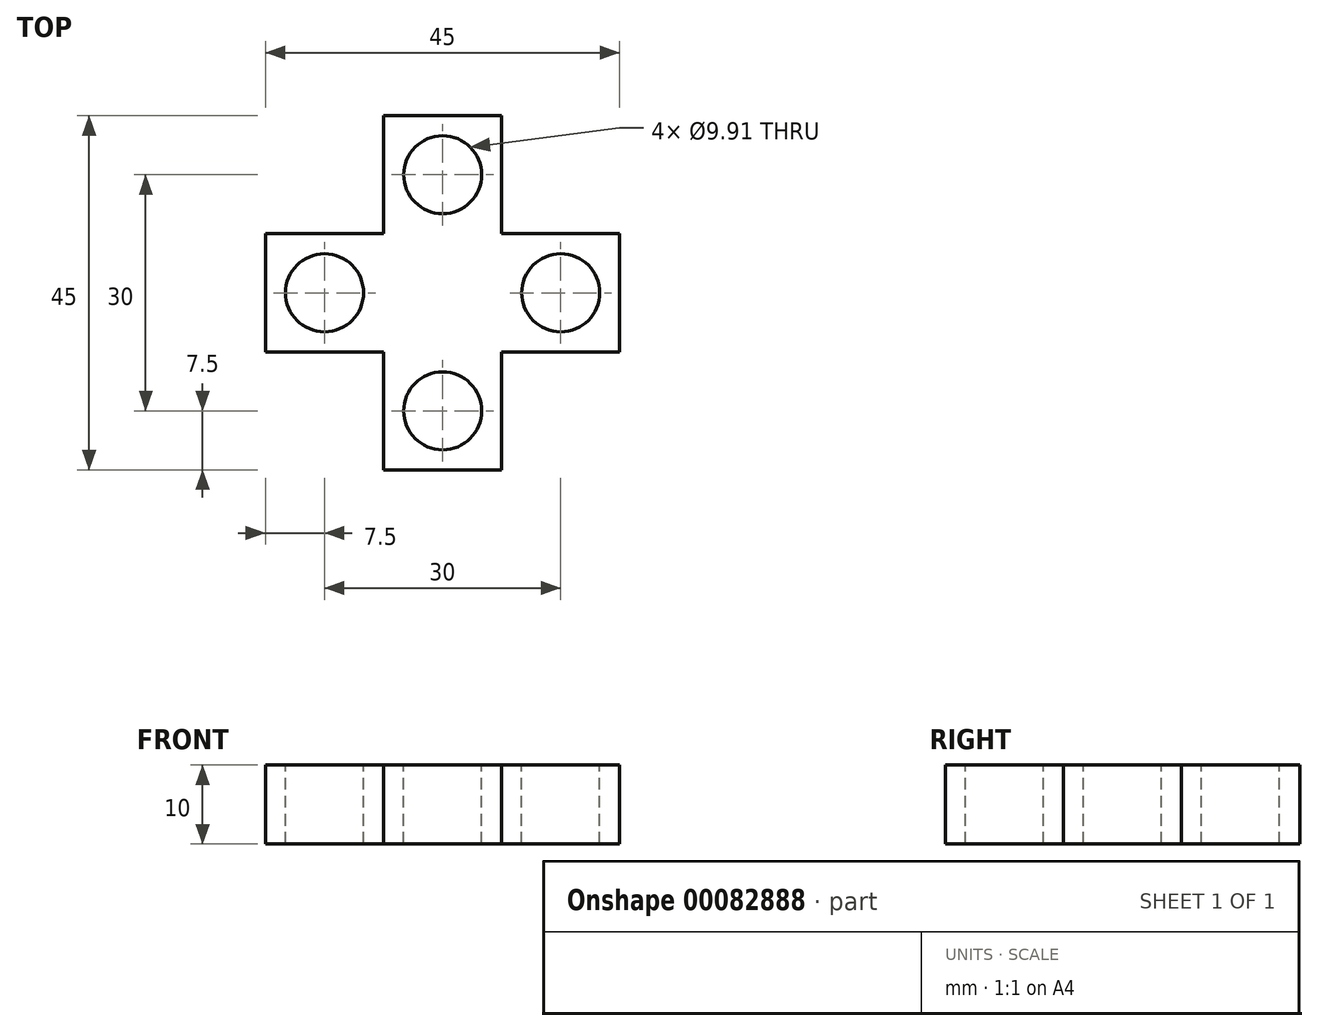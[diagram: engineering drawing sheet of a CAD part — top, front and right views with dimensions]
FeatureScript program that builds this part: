
annotation { "Feature Type Name" : "Feature", "Feature Type Description" : "" }
export const myFeature = defineFeature(function(context is Context, id is Id, definition is map)
    precondition{}
    {
        {
            var Q0;
            Q0=qCreatedBy(makeId("Top.planeOp"),FACE);
            var sketch = newSketch(context, id + "F0", { "sketchPlane" : qUnion([Q0])});
            skLineSegment(sketch, "E0.bottom", {"start": v(22.5, 7.5) * mm, "end": v(-22.5, 7.5) * mm});
            skLineSegment(sketch, "E0.top", {"start": v(22.5, -7.5) * mm, "end": v(-22.5, -7.5) * mm});
            skLineSegment(sketch, "E0.left", {"start": v(22.5, 7.5) * mm, "end": v(22.5, -7.5) * mm});
            skLineSegment(sketch, "E0.right", {"start": v(-22.5, 7.5) * mm, "end": v(-22.5, -7.5) * mm});
            skPoint(sketch, "E0.middle", {"position": v(0, 0) * mm});
            skLineSegment(sketch, "E1.bottom", {"start": v(-7.5, 22.5) * mm, "end": v(7.5, 22.5) * mm});
            skLineSegment(sketch, "E1.top", {"start": v(-7.5, -22.5) * mm, "end": v(7.5, -22.5) * mm});
            skLineSegment(sketch, "E1.left", {"start": v(-7.5, 22.5) * mm, "end": v(-7.5, -22.5) * mm});
            skLineSegment(sketch, "E1.right", {"start": v(7.5, 22.5) * mm, "end": v(7.5, -22.5) * mm});
            skSolve(sketch);
        }
        {
            var Q0;
            {var subQ0=sQuery(id+"F0.wireOp",EDGE,"E0.right");Q0=makeQuery(id+"F0.imprint","IMPRINT",FACE,{"disambiguationData":[TD([[makeQuery(id+"F0.imprint","IMPRINT",EDGE,{"derivedFrom":subQ0}),1.0]])]});}
            var Q1;
            {var subQ0=sQuery(id+"F0.wireOp",EDGE,"E1.right");var subQ1=sQuery(id+"F0.wireOp",EDGE,"E0.bottom");var subQ2=makeQuery(id+"F0.imprint","INTERSECT",VERTEX,{"derivedFrom":[subQ1,subQ0]});Q1=makeQuery(id+"F0.imprint","IMPRINT",FACE,{"disambiguationData":[TD([[makeQuery(id+"F0.imprint","IMPRINT",EDGE,{"disambiguationData":[TD([[subQ2,-1.0]])],"derivedFrom":subQ1}),1.0]])]});}
            var Q2;
            {var subQ0=sQuery(id+"F0.wireOp",EDGE,"E0.left");Q2=makeQuery(id+"F0.imprint","IMPRINT",FACE,{"disambiguationData":[TD([[makeQuery(id+"F0.imprint","IMPRINT",EDGE,{"derivedFrom":subQ0}),-1.0]])]});}
            var Q3;
            {var subQ5=sQuery(id+"F0.wireOp",EDGE,"E1.bottom");Q3=makeQuery(id+"F0.imprint","IMPRINT",FACE,{"disambiguationData":[TD([[makeQuery(id+"F0.imprint","IMPRINT",EDGE,{"derivedFrom":subQ5}),-1.0]])]});}
            var Q4;
            {var subQ5=sQuery(id+"F0.wireOp",EDGE,"E1.top");Q4=makeQuery(id+"F0.imprint","IMPRINT",FACE,{"disambiguationData":[TD([[makeQuery(id+"F0.imprint","IMPRINT",EDGE,{"derivedFrom":subQ5}),1.0]])]});}
            extrude(context, id + "F1", {"entities" : qUnion([Q0, Q1, Q2, Q3, Q4]), "depth" : 10 * mm});
        }
        {
            var Q0;
            Q0=makeQuery(id+"F1.opExtrude","CAP_FACE",FACE,{"disambiguationData":[OSD([sQuery(id+"F0.wireOp",EDGE,"E0.bottom"),sQuery(id+"F0.wireOp",EDGE,"E0.top"),sQuery(id+"F0.wireOp",EDGE,"E0.left"),sQuery(id+"F0.wireOp",EDGE,"E0.right"),sQuery(id+"F0.wireOp",EDGE,"E1.bottom"),sQuery(id+"F0.wireOp",EDGE,"E1.top"),sQuery(id+"F0.wireOp",EDGE,"E1.left"),sQuery(id+"F0.wireOp",EDGE,"E1.right")])],"isStart":false});
            var sketch = newSketch(context, id + "F2", { "sketchPlane" : qUnion([Q0])});
            skCircle(sketch, "E2", {"center": v(-15, 0) * mm, "radius": 4.96 * mm});
            skCircle(sketch, "E3", {"center": v(15, 0) * mm, "radius": 4.96 * mm});
            skCircle(sketch, "E4", {"center": v(0, -15) * mm, "radius": 4.96 * mm});
            skCircle(sketch, "E5", {"center": v(0, 15) * mm, "radius": 4.96 * mm});
            skPoint(sketch, "E6", {"position": v(-22.5, 0) * mm});
            skLineSegment(sketch, "E7", {"start": v(15, -7.5) * mm, "end": v(15, 7.5) * mm, "construction": true});
            skLineSegment(sketch, "E8", {"start": v(-15, -7.5) * mm, "end": v(-15, 7.5) * mm, "construction": true});
            skLineSegment(sketch, "E9", {"start": v(7.5, -15) * mm, "end": v(-7.5, -15) * mm, "construction": true});
            skLineSegment(sketch, "E10", {"start": v(7.5, 15) * mm, "end": v(-7.5, 15) * mm, "construction": true});
            skSolve(sketch);
        }
        {
            var Q0;
            Q0 = qSketchRegion(id + "F2", true);
            extrude(context, id + "F3", {"entities" : qUnion([Q0]), "operationType" : NewBodyOperationType.REMOVE, "endBound" : BoundingType.THROUGH_ALL, "oppositeDirection" : true, "depth" : 25 * mm});
        }
    });
